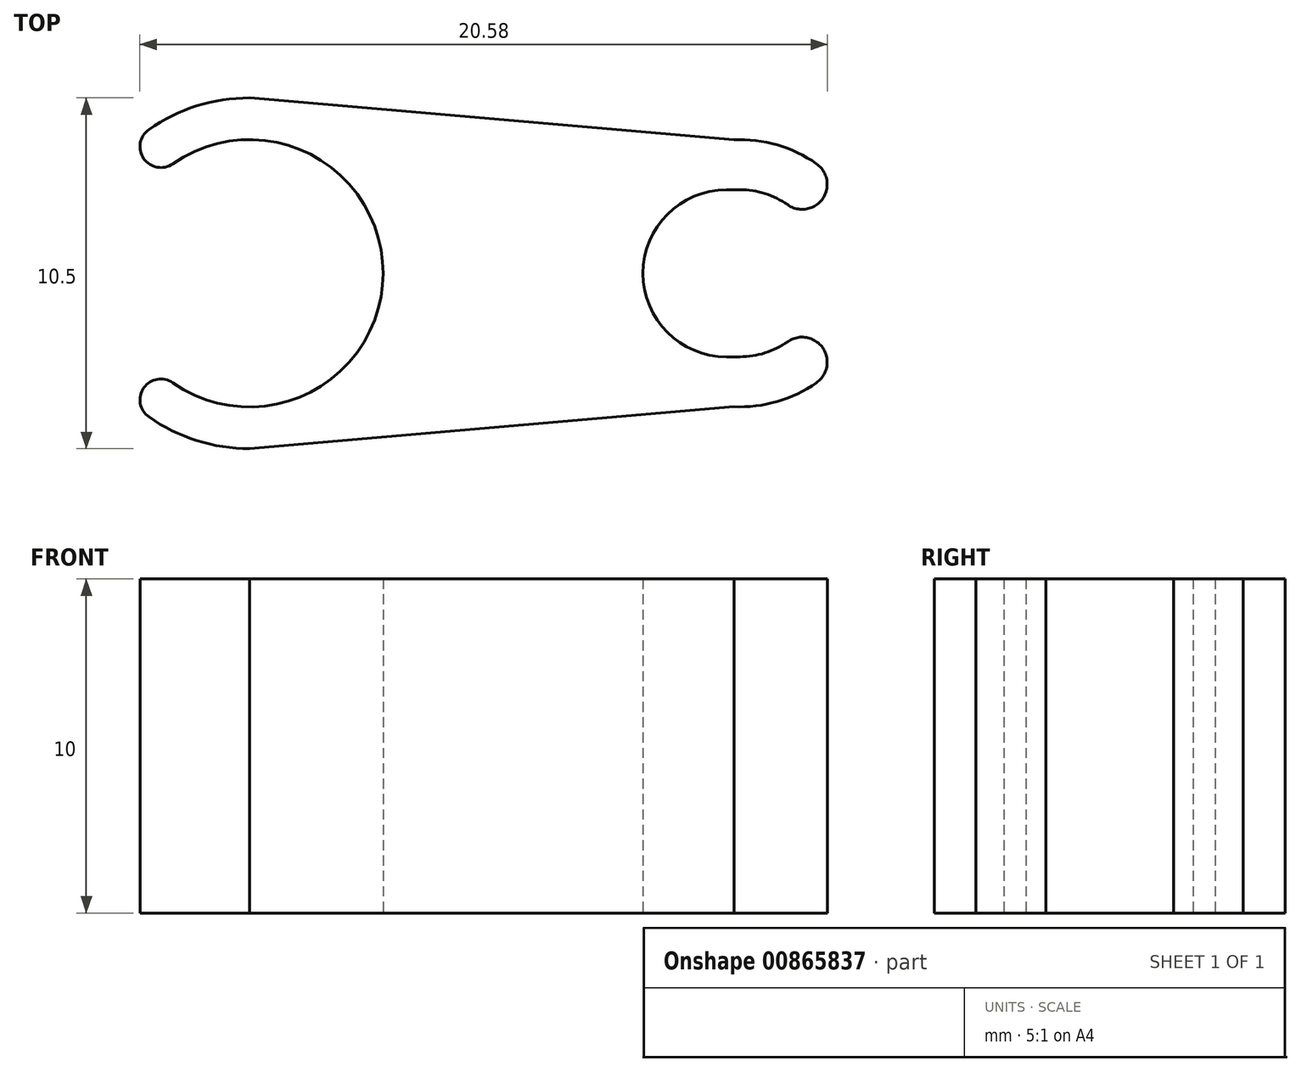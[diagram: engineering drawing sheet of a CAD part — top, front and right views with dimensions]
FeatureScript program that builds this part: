
annotation { "Feature Type Name" : "Feature", "Feature Type Description" : "" }
export const myFeature = defineFeature(function(context is Context, id is Id, definition is map)
    precondition{}
    {
        {
            var Q0;
            Q0=qCreatedBy(makeId("Top.planeOp"),FACE);
            var sketch = newSketch(context, id + "F0", { "sketchPlane" : qUnion([Q0])});
            skArc(sketch, "E0", {"start": v(-2.3, -3.28) * mm, "mid": v(4, 0) * mm, "end": v(-2.3, 3.28) * mm});
            skArc(sketch, "E1", {"start": v(-3.01, -4.3) * mm, "mid": v(-1.14, -5.12) * mm, "end": v(0.9, -5.17) * mm});
            skArc(sketch, "E2", {"start": v(-3.01, 4.3) * mm, "mid": v(-3.16, 3.43) * mm, "end": v(-2.3, 3.28) * mm});
            skArc(sketch, "E3", {"start": v(-2.3, -3.28) * mm, "mid": v(-3.16, -3.43) * mm, "end": v(-3.01, -4.3) * mm});
            skLineSegment(sketch, "E4", {"start": v(0, 5.25) * mm, "end": v(14.5, 4) * mm});
            skLineSegment(sketch, "E5", {"start": v(0, -5.25) * mm, "end": v(14.5, -4) * mm});
            skPoint(sketch, "E6.orphan", {"position": v(14.28, 6.24) * mm});
            skPoint(sketch, "E7.orphan", {"position": v(18, 5.32) * mm});
            skArc(sketch, "E8.trimOffspring", {"start": v(0.9, 5.17) * mm, "mid": v(-1.14, 5.12) * mm, "end": v(-3.01, 4.3) * mm});
            skPoint(sketch, "E9.orphan", {"position": v(14.28, -5.37) * mm});
            skPoint(sketch, "E10.start.orphan", {"position": v(14.28, 2.5) * mm});
            skPoint(sketch, "E11.start.orphan", {"position": v(14.28, -2.5) * mm});
            skLineSegment(sketch, "E12", {"start": v(14.28, 2.5) * mm, "end": v(14.68, 2.5) * mm});
            skLineSegment(sketch, "E13", {"start": v(14.28, -2.5) * mm, "end": v(14.68, -2.5) * mm});
            skArc(sketch, "E14", {"start": v(16.12, 2.05) * mm, "mid": v(15.43, 2.38) * mm, "end": v(14.68, 2.5) * mm});
            skPoint(sketch, "E15.center.orphan", {"position": v(16.15, 2.66) * mm});
            skPoint(sketch, "E16.trimOffspring.end.orphan", {"position": v(14.28, 4.01) * mm});
            skArc(sketch, "E17", {"start": v(14.5, -4) * mm, "mid": v(15.8, -3.84) * mm, "end": v(16.98, -3.28) * mm});
            skPoint(sketch, "E18.endSnap0", {"position": v(18.68, 0) * mm});
            skArc(sketch, "E19", {"start": v(16.12, 2.05) * mm, "mid": v(17.16, 2.23) * mm, "end": v(16.98, 3.28) * mm});
            skArc(sketch, "E20", {"start": v(16.98, -3.28) * mm, "mid": v(17.16, -2.23) * mm, "end": v(16.12, -2.05) * mm});
            skArc(sketch, "E21", {"start": v(14.28, 2.5) * mm, "mid": v(11.78, 0) * mm, "end": v(14.28, -2.5) * mm});
            skArc(sketch, "E22.trimOffspring", {"start": v(14.68, -2.5) * mm, "mid": v(15.43, -2.38) * mm, "end": v(16.12, -2.05) * mm});
            skArc(sketch, "E23.trimOffspring", {"start": v(16.98, 3.28) * mm, "mid": v(15.8, 3.84) * mm, "end": v(14.5, 4) * mm});
            skPoint(sketch, "E18.end.orphan", {"position": v(20.23, 0) * mm});
            skSolve(sketch);
        }
        {
            var Q0;
            Q0=makeQuery(id+"F0.imprint","IMPRINT",FACE,{"disambiguationData":[TD([[makeQuery(id+"F0.imprint","IMPRINT",EDGE,{"derivedFrom":sQuery(id+"F0.wireOp",EDGE,"E0")}),-1.0]])]});
            extrude(context, id + "F1", {"entities" : qUnion([Q0]), "depth" : 10 * mm, "offsetDistance" : 25 * mm});
        }
    });
